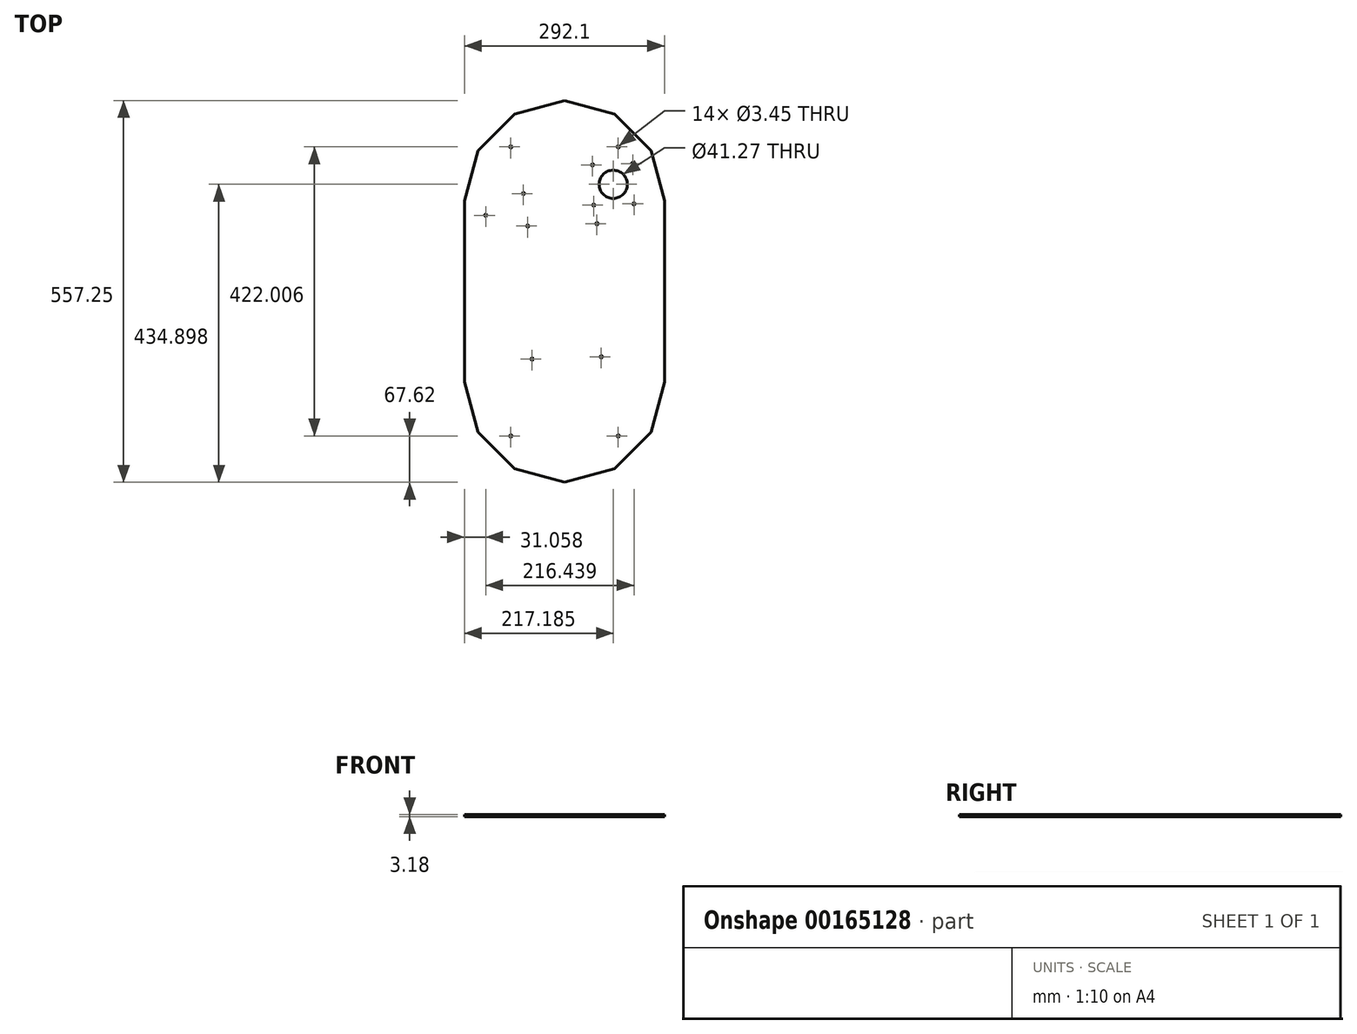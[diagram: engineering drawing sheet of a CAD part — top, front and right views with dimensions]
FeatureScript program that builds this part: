
annotation { "Feature Type Name" : "Feature", "Feature Type Description" : "" }
export const myFeature = defineFeature(function(context is Context, id is Id, definition is map)
    precondition{}
    {
        {
            var Q0;
            Q0=qCreatedBy(makeId("Top.planeOp"),FACE);
            var sketch = newSketch(context, id + "F0", { "sketchPlane" : qUnion([Q0])});
            skLineSegment(sketch, "E0", {"start": v(146.05, 0) * mm, "end": v(292.1, 0) * mm, "construction": true});
            skLineSegment(sketch, "E1", {"start": v(146.05, 0) * mm, "end": v(272.53, 73.03) * mm, "construction": true});
            skLineSegment(sketch, "E2", {"start": v(146.05, 0) * mm, "end": v(219.08, 126.48) * mm, "construction": true});
            skLineSegment(sketch, "E3", {"start": v(146.05, 0) * mm, "end": v(146.05, 146.05) * mm, "construction": true});
            skLineSegment(sketch, "E4", {"start": v(292.1, 0) * mm, "end": v(272.53, 73.03) * mm});
            skLineSegment(sketch, "E5", {"start": v(272.53, 73.03) * mm, "end": v(219.07, 126.48) * mm});
            skLineSegment(sketch, "E6", {"start": v(219.08, 126.48) * mm, "end": v(146.05, 146.05) * mm});
            skLineSegment(sketch, "E7", {"start": v(292.1, 0) * mm, "end": v(292.1, -265.15) * mm});
            skLineSegment(sketch, "E8", {"start": v(292.1, -265.15) * mm, "end": v(146.05, -265.15) * mm, "construction": true});
            skLineSegment(sketch, "E9", {"start": v(146.05, -265.15) * mm, "end": v(272.53, -338.18) * mm, "construction": true});
            skLineSegment(sketch, "E10", {"start": v(146.05, 0) * mm, "end": v(73.03, 126.48) * mm, "construction": true});
            skLineSegment(sketch, "E11", {"start": v(146.05, 0) * mm, "end": v(19.57, 73.02) * mm, "construction": true});
            skLineSegment(sketch, "E12", {"start": v(146.05, 0) * mm, "end": v(0, 0) * mm, "construction": true});
            skLineSegment(sketch, "E13", {"start": v(146.05, -265.15) * mm, "end": v(0, -265.15) * mm, "construction": true});
            skLineSegment(sketch, "E14", {"start": v(146.05, 146.05) * mm, "end": v(73.02, 126.48) * mm});
            skLineSegment(sketch, "E15", {"start": v(73.03, 126.48) * mm, "end": v(19.57, 73.03) * mm});
            skLineSegment(sketch, "E16", {"start": v(19.57, 73.03) * mm, "end": v(0, 0) * mm});
            skLineSegment(sketch, "E17", {"start": v(0, 0) * mm, "end": v(0, -265.15) * mm});
            skLineSegment(sketch, "E18", {"start": v(146.05, -265.15) * mm, "end": v(219.08, -391.64) * mm, "construction": true});
            skLineSegment(sketch, "E19", {"start": v(146.05, -265.15) * mm, "end": v(146.05, -411.2) * mm, "construction": true});
            skLineSegment(sketch, "E20", {"start": v(146.05, -265.15) * mm, "end": v(73.03, -391.64) * mm, "construction": true});
            skLineSegment(sketch, "E21", {"start": v(146.05, -265.15) * mm, "end": v(19.57, -338.18) * mm, "construction": true});
            skLineSegment(sketch, "E22", {"start": v(0, -265.15) * mm, "end": v(19.57, -338.18) * mm});
            skLineSegment(sketch, "E23", {"start": v(19.57, -338.18) * mm, "end": v(73.03, -391.64) * mm});
            skLineSegment(sketch, "E24", {"start": v(73.03, -391.64) * mm, "end": v(146.05, -411.2) * mm});
            skLineSegment(sketch, "E25", {"start": v(146.05, -411.2) * mm, "end": v(219.08, -391.64) * mm});
            skLineSegment(sketch, "E26", {"start": v(219.08, -391.64) * mm, "end": v(272.53, -338.18) * mm});
            skLineSegment(sketch, "E27", {"start": v(272.53, -338.18) * mm, "end": v(292.1, -265.15) * mm});
            skLineSegment(sketch, "E28", {"start": v(146.05, 0) * mm, "end": v(146.05, -132.58) * mm, "construction": true});
            skLineSegment(sketch, "E29", {"start": v(146.05, -132.58) * mm, "end": v(146.05, -265.15) * mm, "construction": true});
            skSolve(sketch);
        }
        {
            var Q0;
            Q0=qSketchRegion(id+"F0",true);
            extrude(context, id + "F1", {"entities" : qUnion([Q0]), "depth" : 3.17 * mm});
        }
        {
            var Q0;
            Q0=makeQuery(id+"F1.opExtrude","CAP_FACE",FACE,{"disambiguationData":[OSD([sQuery(id+"F0.wireOp",EDGE,"E4"),sQuery(id+"F0.wireOp",EDGE,"E5"),sQuery(id+"F0.wireOp",EDGE,"E6"),sQuery(id+"F0.wireOp",EDGE,"E7"),sQuery(id+"F0.wireOp",EDGE,"E14"),sQuery(id+"F0.wireOp",EDGE,"E15"),sQuery(id+"F0.wireOp",EDGE,"E16"),sQuery(id+"F0.wireOp",EDGE,"E17"),sQuery(id+"F0.wireOp",EDGE,"E22"),sQuery(id+"F0.wireOp",EDGE,"E23"),sQuery(id+"F0.wireOp",EDGE,"E24"),sQuery(id+"F0.wireOp",EDGE,"E25"),sQuery(id+"F0.wireOp",EDGE,"E26"),sQuery(id+"F0.wireOp",EDGE,"E27")])],"isStart":false});
            var sketch = newSketch(context, id + "F2", { "sketchPlane" : qUnion([Q0])});
            skLineSegment(sketch, "E30", {"start": v(146.05, 119.75) * mm, "end": v(205.93, 103.7) * mm, "construction": true});
            skLineSegment(sketch, "E31.bottom", {"start": v(245.58, 54.01) * mm, "end": v(186.87, 52.1) * mm, "construction": true});
            skLineSegment(sketch, "E31.top", {"start": v(247.5, -4.7) * mm, "end": v(188.8, -6.61) * mm, "construction": true});
            skLineSegment(sketch, "E31.left", {"start": v(245.58, 54.01) * mm, "end": v(247.5, -4.7) * mm, "construction": true});
            skLineSegment(sketch, "E31.right", {"start": v(186.87, 52.1) * mm, "end": v(188.8, -6.61) * mm, "construction": true});
            skPoint(sketch, "E31.middle", {"position": v(217.19, 23.7) * mm});
            skCircle(sketch, "E32", {"center": v(217.19, 23.7) * mm, "radius": 20.64 * mm});
            skLineSegment(sketch, "E33", {"start": v(146.05, -132.58) * mm, "end": v(92.31, -37.13) * mm, "construction": true});
            skLineSegment(sketch, "E34", {"start": v(142.88, -35.48) * mm, "end": v(193.44, -33.82) * mm, "construction": true});
            skLineSegment(sketch, "E35", {"start": v(193.44, -33.82) * mm, "end": v(146.05, -132.58) * mm, "construction": true});
            skLineSegment(sketch, "E36", {"start": v(146.05, -132.58) * mm, "end": v(98.66, -231.33) * mm, "construction": true});
            skLineSegment(sketch, "E37", {"start": v(199.79, -228.03) * mm, "end": v(146.05, -132.58) * mm, "construction": true});
            skCircle(sketch, "E38", {"center": v(92.31, -37.13) * mm, "radius": 1.73 * mm});
            skCircle(sketch, "E39", {"center": v(193.44, -33.82) * mm, "radius": 1.73 * mm});
            skCircle(sketch, "E40", {"center": v(188.8, -6.61) * mm, "radius": 1.73 * mm});
            skCircle(sketch, "E41", {"center": v(247.5, -4.7) * mm, "radius": 1.73 * mm});
            skCircle(sketch, "E42", {"center": v(245.58, 54.01) * mm, "radius": 1.73 * mm});
            skCircle(sketch, "E43", {"center": v(186.87, 52.1) * mm, "radius": 1.73 * mm});
            skCircle(sketch, "E44", {"center": v(199.79, -228.03) * mm, "radius": 1.73 * mm});
            skCircle(sketch, "E45", {"center": v(98.66, -231.33) * mm, "radius": 1.73 * mm});
            skLineSegment(sketch, "E46", {"start": v(146.05, -132.58) * mm, "end": v(142.88, -35.48) * mm, "construction": true});
            skLineSegment(sketch, "E47", {"start": v(146.05, -132.58) * mm, "end": v(149.22, -229.68) * mm, "construction": true});
            skLineSegment(sketch, "E48", {"start": v(149.22, -229.68) * mm, "end": v(199.79, -228.03) * mm, "construction": true});
            skLineSegment(sketch, "E49", {"start": v(149.22, -229.68) * mm, "end": v(98.66, -231.33) * mm, "construction": true});
            skLineSegment(sketch, "E50", {"start": v(142.88, -35.48) * mm, "end": v(92.31, -37.13) * mm, "construction": true});
            skLineSegment(sketch, "E51", {"start": v(205.93, 103.7) * mm, "end": v(249.76, 59.88) * mm, "construction": true});
            skLineSegment(sketch, "E52", {"start": v(175.99, 111.73) * mm, "end": v(182.56, 136.27) * mm, "construction": true});
            skLineSegment(sketch, "E53", {"start": v(227.84, 81.8) * mm, "end": v(245.8, 99.75) * mm, "construction": true});
            skLineSegment(sketch, "E54", {"start": v(146.05, 146.05) * mm, "end": v(146.05, 119.75) * mm, "construction": true});
            skLineSegment(sketch, "E55", {"start": v(146.05, -132.58) * mm, "end": v(222.2, -130.09) * mm, "construction": true});
            skLineSegment(sketch, "E56", {"start": v(222.2, -130.09) * mm, "end": v(217.19, 23.7) * mm, "construction": true});
            skCircle(sketch, "E57", {"center": v(224.48, 78.43) * mm, "radius": 1.73 * mm});
            skLineSegment(sketch, "E58.bottom", {"start": v(224.48, 78.43) * mm, "end": v(67.62, 78.43) * mm, "construction": true});
            skLineSegment(sketch, "E58.top", {"start": v(224.48, -343.58) * mm, "end": v(67.62, -343.58) * mm, "construction": true});
            skLineSegment(sketch, "E58.left", {"start": v(224.48, 78.43) * mm, "end": v(224.48, -343.58) * mm, "construction": true});
            skLineSegment(sketch, "E58.right", {"start": v(67.62, 78.43) * mm, "end": v(67.62, -343.58) * mm, "construction": true});
            skPoint(sketch, "E58.middle", {"position": v(146.05, -132.58) * mm});
            skCircle(sketch, "E59", {"center": v(67.62, 78.43) * mm, "radius": 1.73 * mm});
            skCircle(sketch, "E60", {"center": v(67.62, -343.58) * mm, "radius": 1.73 * mm});
            skCircle(sketch, "E61", {"center": v(224.48, -343.58) * mm, "radius": 1.73 * mm});
            skLineSegment(sketch, "E62", {"start": v(0, -132.58) * mm, "end": v(292.1, -132.58) * mm, "construction": true});
            skCircle(sketch, "E63", {"center": v(224.48, 78.43) * mm, "radius": 4.76 * mm, "construction": true});
            skLineSegment(sketch, "E64", {"start": v(199.79, -228.03) * mm, "end": v(193.44, -33.82) * mm, "construction": true});
            skLineSegment(sketch, "E65", {"start": v(92.31, -37.13) * mm, "end": v(98.66, -231.33) * mm, "construction": true});
            skLineSegment(sketch, "E66", {"start": v(0, 0) * mm, "end": v(31.06, 0) * mm, "construction": true});
            skLineSegment(sketch, "E67", {"start": v(31.06, 0) * mm, "end": v(31.06, -21.49) * mm, "construction": true});
            skCircle(sketch, "E68", {"center": v(31.06, -21.49) * mm, "radius": 1.73 * mm});
            skLineSegment(sketch, "E69", {"start": v(31.06, -21.49) * mm, "end": v(86.05, 10.26) * mm, "construction": true});
            skCircle(sketch, "E70", {"center": v(86.05, 10.26) * mm, "radius": 1.73 * mm});
            skCircle(sketch, "E71", {"center": v(245.58, 54.01) * mm, "radius": 5.56 * mm, "construction": true});
            skLineSegment(sketch, "E72", {"start": v(224.48, 78.43) * mm, "end": v(227.84, 81.8) * mm, "construction": true});
            skLineSegment(sketch, "E73", {"start": v(249.76, 59.88) * mm, "end": v(265.8, 0) * mm, "construction": true});
            skSolve(sketch);
        }
        {
            var Q0;
            Q0=qSketchRegion(id+"F2",true);
            var Q1;
            Q1=makeQuery(id+"F1.opExtrude","CAP_FACE",FACE,{"disambiguationData":[OSD([sQuery(id+"F0.wireOp",EDGE,"E4"),sQuery(id+"F0.wireOp",EDGE,"E5"),sQuery(id+"F0.wireOp",EDGE,"E6"),sQuery(id+"F0.wireOp",EDGE,"E7"),sQuery(id+"F0.wireOp",EDGE,"E14"),sQuery(id+"F0.wireOp",EDGE,"E15"),sQuery(id+"F0.wireOp",EDGE,"E16"),sQuery(id+"F0.wireOp",EDGE,"E17"),sQuery(id+"F0.wireOp",EDGE,"E22"),sQuery(id+"F0.wireOp",EDGE,"E23"),sQuery(id+"F0.wireOp",EDGE,"E24"),sQuery(id+"F0.wireOp",EDGE,"E25"),sQuery(id+"F0.wireOp",EDGE,"E26"),sQuery(id+"F0.wireOp",EDGE,"E27")])],"isStart":true});
            extrude(context, id + "F3", {"entities" : qUnion([Q0]), "operationType" : NewBodyOperationType.REMOVE, "endBound" : BoundingType.UP_TO_SURFACE, "oppositeDirection" : true, "endBoundEntityFace" : qUnion([Q1]), "depth" : 25.4 * mm});
        }
    });
